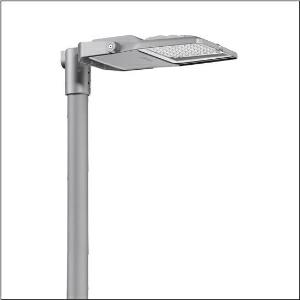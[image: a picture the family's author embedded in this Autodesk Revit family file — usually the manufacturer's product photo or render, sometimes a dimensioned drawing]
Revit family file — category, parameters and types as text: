
# Revit family: floodlight_fl_21_iq_mini___pl64_5xa7771c2e3a_b06c
name_source: partatom
category: Lighting Fixtures
units: mm (PartAtom-declared; Revit-internal decimal feet)

## family parameters
Cut with Voids When Loaded = No
Host = Face
Light Source = No
Part Type = Normal
Room Calculation Point = No
Round Connector Dimension = Use Diameter
Shared = No

## types (1)
- --- (1 x LED, 11790 lm, 87.2 W, 3000K)
    Apparent Load = 87 VA
    CIE Flux Codes = 28 80 98 100 100
    Color Rendering = 70
    Color Temperature = 3000K
    Default Elevation = 1800 mm
    Description = Floodlight FL 21 iQ mini, floodlight, primary light control with lens, of PMMA, primary optical cover: protective disc, of toughened safety glass, transparent, light distribution: PL64, light emission: direct distribution, installation type: surface-mounted, LED, High Power LED, rated luminous flux: 11.790lm, luminous efficacy: 135lm/W, light colour: 730, colour temperature: 3000K, control: Auto-Match, Temp-Guard, Lumen-Switch, Night-Set, Smart-Wire, Light-Fading, Desk-Remote (wireless, voltage-free reading and setting of iQ features in the workshop via application-optimized NFC function/RFID function), optimised constant luminous flux control (CLO 2.0), with terminal, 6-pole, mains connection: 220..240V, AC, 50/60Hz, start of lifetime: 87W, end of service life: 92W, reduction: 40W, luminaire housing, of diecast aluminium, powder-coated, Siteco® metallic grey (DB 702S), corrosivity category C5 mid according to DIN EN ISO 12944, sealing non-destructively replaceable, please order mast flange separately, mast bracket, of steel, galvanised, powder-coated, Siteco® metallic grey (DB 702S), protection rating (complete): IP66, insulation class (complete): insulation class II (safety insulation), certification: CE, ENEC, VDE, protection symbol: D, impact resistance: IK08, permissible operating ambient temperature: -40..+40°C, permissible operating ambient temperature for outdoor applications: -40..+50°C, standard: DIN EN 12944, LABS conformity tested according to VDMA 24364:2018-05, packaging unit: 1 piece

Light Distribution: PL64
    Height = 70 mm
    Lamp = 1 x LED
    Lamp Light Flux = 11790 lm
    Lamp Power = 87.2 W
    Lamp count = 1
    Length = 485 mm
    Luminous efficacy = 135 lm/W
    Manufacturer = Siteco
    ModVariant = No
    Model = 5XA7771C2E3A
    Number of Poles = 1
    OnlyDefault = Yes
    Power Factor = 1
    Product Name = Floodlight FL 21 iQ mini | PL64
    Product group = floodlight | pylon annexe
    ProductGroupID = 6200
    Protection Class = Protection class II
    Protection Degree = IP 66
    RLX_Detail_Level = 1
    RLX_Emergency_Light_Flux = 0 lm
    RLX_Emergency_Type = 0
    RLX_Emergency_Type_DB = No
    RlxData = <blob elided: 101337 chars, md5=3cbba5c7>
    Socket = socket
    Standby Power = 0 W
    System Light Flux = 11790 lm
    System Power = 87 W
    Type Comments = factory setting: luminous flux: 100 % | dim-lin: 254 | 456 mA
    Type Image = l_1007125.jpg
    URL = http://relux.com
    VarID = @adj_136947
    Voltage = 0 V
    Weight = 0.00 kg
    Width = 337 mm

## geometry (parser evidence)
native form markers: Blend x4, Sweep x11
no freeform markers — native parametric forms only
